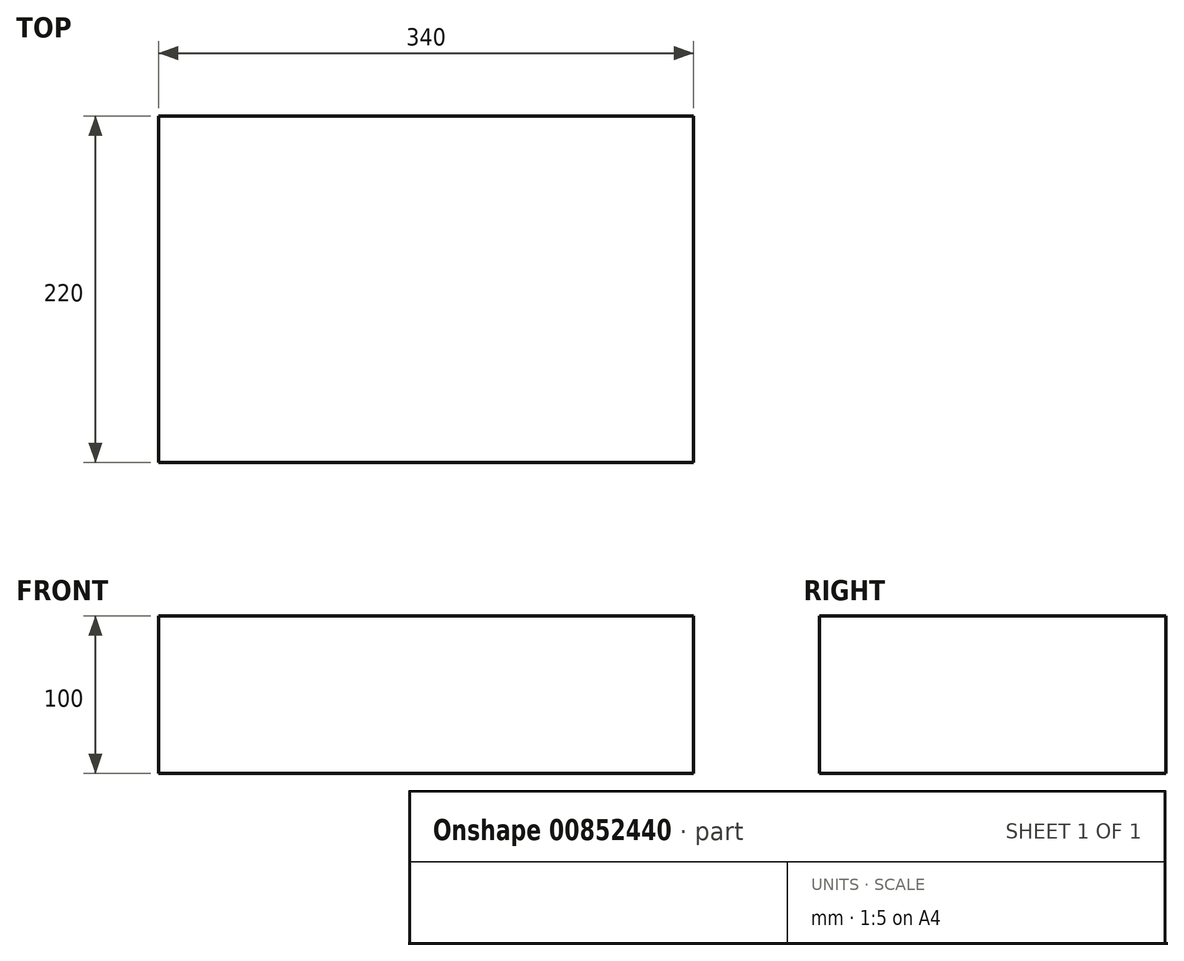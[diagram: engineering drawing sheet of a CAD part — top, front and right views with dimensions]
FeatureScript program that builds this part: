
annotation { "Feature Type Name" : "Feature", "Feature Type Description" : "" }
export const myFeature = defineFeature(function(context is Context, id is Id, definition is map)
    precondition{}
    {
        {
            var Q0;
            Q0=qCreatedBy(makeId("Top.planeOp"),FACE);
            var sketch = newSketch(context, id + "F0", { "sketchPlane" : qUnion([Q0])});
            skLineSegment(sketch, "E0.bottom", {"start": v(170, -110) * mm, "end": v(-170, -110) * mm});
            skLineSegment(sketch, "E0.top", {"start": v(170, 110) * mm, "end": v(-170, 110) * mm});
            skLineSegment(sketch, "E0.left", {"start": v(170, -110) * mm, "end": v(170, 110) * mm});
            skLineSegment(sketch, "E0.right", {"start": v(-170, -110) * mm, "end": v(-170, 110) * mm});
            skPoint(sketch, "E0.middle", {"position": v(0, 0) * mm});
            skSolve(sketch);
        }
        {
            var Q0;
            Q0=makeQuery(id+"F0.imprint","IMPRINT",FACE,{"disambiguationData":[TD([[makeQuery(id+"F0.imprint","IMPRINT",EDGE,{"derivedFrom":sQuery(id+"F0.wireOp",EDGE,"E0.bottom")}),-1.0]])]});
            extrude(context, id + "F1", {"entities" : qUnion([Q0]), "depth" : 100 * mm, "offsetDistance" : 25 * mm});
        }
    });
